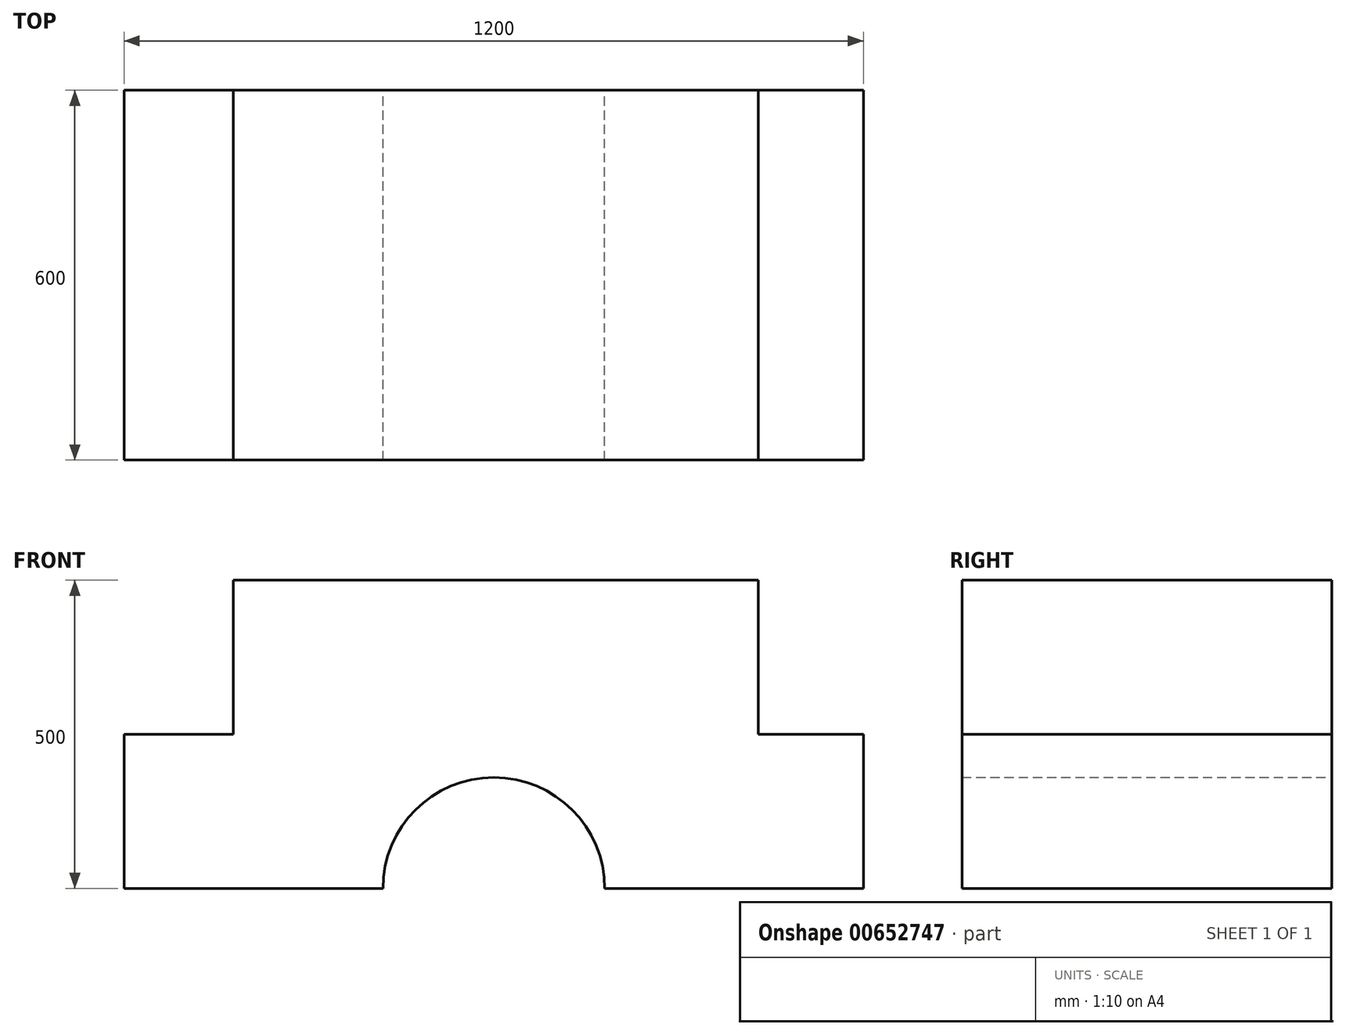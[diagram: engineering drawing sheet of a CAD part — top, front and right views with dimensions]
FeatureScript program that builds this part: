
annotation { "Feature Type Name" : "Feature", "Feature Type Description" : "" }
export const myFeature = defineFeature(function(context is Context, id is Id, definition is map)
    precondition{}
    {
        {
            var Q0;
            Q0=qCreatedBy(makeId("Front.planeOp"),FACE);
            var sketch = newSketch(context, id + "F0", { "sketchPlane" : qUnion([Q0])});
            skLineSegment(sketch, "E0.bottom", {"start": v(429.5, 196.03) * mm, "end": v(-423.04, 196.03) * mm});
            skLineSegment(sketch, "E0.top", {"start": v(600, -303.97) * mm, "end": v(180, -303.97) * mm});
            skLineSegment(sketch, "E0.left", {"start": v(600, -53.97) * mm, "end": v(600, -303.97) * mm});
            skLineSegment(sketch, "E0.right", {"start": v(-600, -53.97) * mm, "end": v(-600, -303.97) * mm});
            skPoint(sketch, "E0.middle", {"position": v(0, -53.97) * mm});
            skArc(sketch, "E1", {"start": v(180, -303.97) * mm, "mid": v(0, -123.97) * mm, "end": v(-180, -303.97) * mm});
            skLineSegment(sketch, "E2.trimOffspring", {"start": v(-180, -303.97) * mm, "end": v(-600, -303.97) * mm});
            skLineSegment(sketch, "E3", {"start": v(-423.04, 196.03) * mm, "end": v(-423.04, -53.97) * mm});
            skPoint(sketch, "E4.orphan", {"position": v(-600, 196.03) * mm});
            skLineSegment(sketch, "E5", {"start": v(-600, -53.97) * mm, "end": v(-423.04, -53.97) * mm});
            skLineSegment(sketch, "E6", {"start": v(429.5, 196.03) * mm, "end": v(429.5, -53.97) * mm});
            skLineSegment(sketch, "E7", {"start": v(429.5, -53.97) * mm, "end": v(600, -53.97) * mm});
            skPoint(sketch, "E8.orphan", {"position": v(600, 196.03) * mm});
            skSolve(sketch);
        }
        {
            var Q0;
            Q0=makeQuery(id+"F0.imprint","IMPRINT",FACE,{"disambiguationData":[TD([[makeQuery(id+"F0.imprint","IMPRINT",EDGE,{"derivedFrom":sQuery(id+"F0.wireOp",EDGE,"E0.bottom")}),1.0]])]});
            extrude(context, id + "F1", {"entities" : qUnion([Q0]), "depth" : 600 * mm, "offsetDistance" : 25 * mm});
        }
    });
